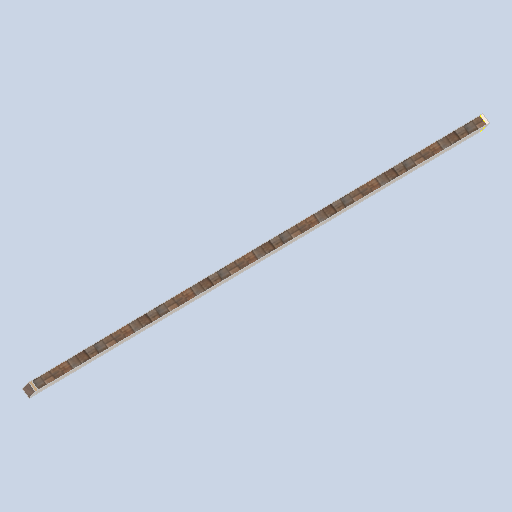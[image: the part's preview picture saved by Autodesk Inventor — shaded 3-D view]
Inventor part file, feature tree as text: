
AUTODESK INVENTOR PART (.ipt)
format: ipt  version: 2024.2 (Build 282272000, 272)  size: 134,656 bytes
history: native  units: in
note: dims shown in document units (in); Inventor stores cm internally (conversion verified against a paired STEP export)
features: sketch x5, other x3, plane x2
ambient origin geometry x8: Origin, YZ Plane, XZ Plane, XY Plane, X Axis, Y Axis, Z Axis, Center Point
bodies: Solid1 (feature_tree)
feature tree (10):
  other  "support_beam_segment_0106.ipt"
  other  "Solid1::support_beam_segment_0106.ipt"
  other  "TaggingFeature1"
  sketch  "Sketch1"  dims[d0=0.3937in]
  sketch  "Sketch2"
  sketch  "Sketch3"
  sketch  "Sketch4"
  sketch  "Sketch5"
  plane  "Work Plane1"
  plane  "Work Plane2"
